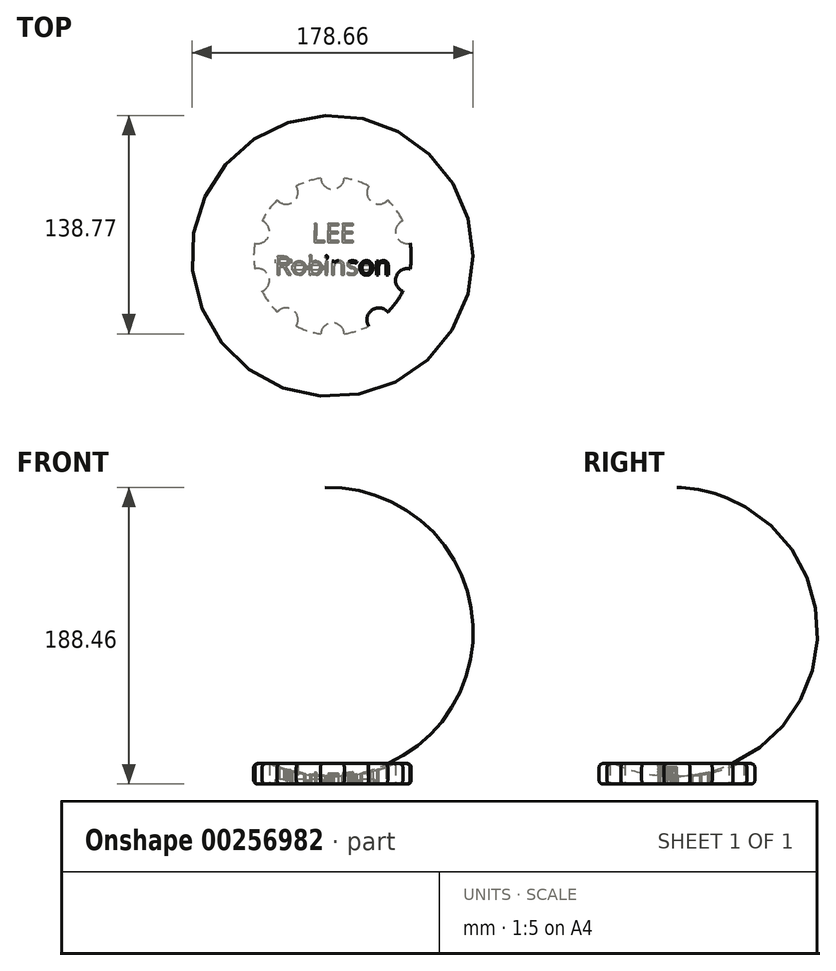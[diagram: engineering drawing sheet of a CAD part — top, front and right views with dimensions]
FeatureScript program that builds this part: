
annotation { "Feature Type Name" : "Feature", "Feature Type Description" : "" }
export const myFeature = defineFeature(function(context is Context, id is Id, definition is map)
    precondition{}
    {
        {
            var Q0;
            Q0=qCreatedBy(makeId("Front.planeOp"),FACE);
            var sketch = newSketch(context, id + "F0", { "sketchPlane" : qUnion([Q0])});
            skLineSegment(sketch, "E0", {"start": v(0, 0) * mm, "end": v(0, 5) * mm});
            skLineSegment(sketch, "E1", {"start": v(-40.53, 13.02) * mm, "end": v(-47.5, 13.02) * mm});
            skLineSegment(sketch, "E2", {"start": v(-50, 10.52) * mm, "end": v(-50, 2.5) * mm});
            skLineSegment(sketch, "E3", {"start": v(-47.5, 0) * mm, "end": v(0, 0) * mm});
            skPoint(sketch, "E4.visualSharp", {"position": v(-50, 13.02) * mm});
            skArc(sketch, "E4.filletArc", {"start": v(-47.5, 13.02) * mm, "mid": v(-49.27, 12.29) * mm, "end": v(-50, 10.52) * mm});
            skPoint(sketch, "E5.visualSharp", {"position": v(-50, 0) * mm});
            skArc(sketch, "E5.filletArc", {"start": v(-50, 2.5) * mm, "mid": v(-49.27, 0.73) * mm, "end": v(-47.5, 0) * mm});
            skArc(sketch, "E6", {"start": v(-39.52, 12.8) * mm, "mid": v(-20.2, 6.7) * mm, "end": v(0, 5) * mm});
            skPoint(sketch, "E7.visualSharp", {"position": v(-40, 13.02) * mm});
            skArc(sketch, "E7.filletArc", {"start": v(-39.52, 12.8) * mm, "mid": v(-40.02, 12.96) * mm, "end": v(-40.53, 13.02) * mm});
            skSolve(sketch);
        }
        {
            var Q0;
            Q0=makeQuery(id+"F0.imprint","IMPRINT",FACE,{"disambiguationData":[TD([[makeQuery(id+"F0.imprint","IMPRINT",EDGE,{"derivedFrom":sQuery(id+"F0.wireOp",EDGE,"E0")}),1.0]])]});
            var Q1;
            Q1=sQuery(id+"F0.wireOp",EDGE,"E0");
            revolve(context, id + "F1", {"entities" : qUnion([Q0]), "axis" : qUnion([Q1]), "revolveType" : RevolveType.FULL});
        }
        {
            var Q0;
            Q0=qCreatedBy(makeId("Top.planeOp"),FACE);
            var sketch = newSketch(context, id + "F2", { "sketchPlane" : qUnion([Q0])});
            skCircle(sketch, "E8", {"center": v(0, -49.99) * mm, "radius": 7.5 * mm});
            skSolve(sketch);
        }
        {
            var Q0;
            Q0=makeQuery(id+"F2.imprint","IMPRINT",FACE,{"disambiguationData":[TD([[makeQuery(id+"F2.imprint","IMPRINT",EDGE,{"derivedFrom":sQuery(id+"F2.wireOp",EDGE,"E8")}),1.0]])]});
            extrude(context, id + "F3", {"entities" : qUnion([Q0]), "operationType" : NewBodyOperationType.REMOVE, "endBound" : BoundingType.THROUGH_ALL, "depth" : 25 * mm});
        }
        {
            var Q0;
            Q0=qCreatedBy(makeId("Front.planeOp"),FACE);
            var sketch = newSketch(context, id + "F4", { "sketchPlane" : qUnion([Q0])});
            skLineSegment(sketch, "E9", {"start": v(0, 0) * mm, "end": v(0, 40.22) * mm});
            skSolve(sketch);
        }
        {
            var Q0;
            Q0=makeQuery(id+"F3.boolean.opBoolean","COPY",FACE,{"derivedFrom":makeQuery(id+"F3.opExtrude","SWEPT_FACE",FACE,{"disambiguationData":[OSD([sQuery(id+"F2.wireOp",EDGE,"E8")])]})});
            var Q1;
            Q1=sQuery(id+"F4.wireOp",EDGE,"E9");
            circularPattern(context, id + "F5", {"patternType" : PatternType.FACE, "faces" : qUnion([Q0]), "axis" : qUnion([Q1]), "angle" : 360 * degree, "instanceCount" : 10, "oppositeDirection" : true, "equalSpace" : true});
        }
        {
            var Q0;
            Q0=qCreatedBy(makeId("Top.planeOp"),FACE);
            var sketch = newSketch(context, id + "F6", { "sketchPlane" : qUnion([Q0])});
            skText(sketch, "E10", { "text": "LEE", "fontName": "OpenSans-Regular.ttf"});
            const initialGuessF6  = {"E10": [-0.01318, 0.0087, 1, 0, 0.012]};
            skSetInitialGuess(sketch, initialGuessF6);
            skSolve(sketch);
        }
        {
            var Q0;
            Q0=qCreatedBy(makeId("Top.planeOp"),FACE);
            var sketch = newSketch(context, id + "F7", { "sketchPlane" : qUnion([Q0])});
            skText(sketch, "E11", { "text": "Robinson\n", "fontName": "OpenSans-Regular.ttf"});
            const initialGuessF7  = {"E11": [-0.0365, -0.012, 1, 0, 0.012]};
            skSetInitialGuess(sketch, initialGuessF7);
            skSolve(sketch);
        }
        {
            var Q0;
            Q0 = qSketchRegion(id + "F6", true);
            extrude(context, id + "F8", {"entities" : qUnion([Q0]), "operationType" : NewBodyOperationType.REMOVE, "depth" : 25 * mm});
        }
        {
            var Q0;
            Q0 = qSketchRegion(id + "F7", true);
            extrude(context, id + "F9", {"entities" : qUnion([Q0]), "operationType" : NewBodyOperationType.REMOVE, "depth" : 25 * mm});
        }
        {
            var Q0;
            Q0=qCreatedBy(makeId("Top.planeOp"),FACE);
            var sketch = newSketch(context, id + "F10", { "sketchPlane" : qUnion([Q0])});
            skLineSegment(sketch, "E12.bottom", {"start": v(26.57, -6.13) * mm, "end": v(16.68, -6.13) * mm});
            skLineSegment(sketch, "E12.top", {"start": v(26.57, -8.94) * mm, "end": v(16.68, -8.94) * mm});
            skLineSegment(sketch, "E12.left", {"start": v(26.57, -6.13) * mm, "end": v(26.57, -8.94) * mm});
            skLineSegment(sketch, "E12.right", {"start": v(16.68, -6.13) * mm, "end": v(16.68, -8.94) * mm});
            skLineSegment(sketch, "E13.bottom", {"start": v(-6.14, -6.02) * mm, "end": v(-15.47, -6.02) * mm});
            skLineSegment(sketch, "E13.top", {"start": v(-6.14, -8.94) * mm, "end": v(-15.47, -8.94) * mm});
            skLineSegment(sketch, "E13.left", {"start": v(-6.14, -6.02) * mm, "end": v(-6.14, -8.94) * mm});
            skLineSegment(sketch, "E13.right", {"start": v(-15.47, -6.02) * mm, "end": v(-15.47, -8.94) * mm});
            skLineSegment(sketch, "E14.bottom", {"start": v(-16.6, -6.02) * mm, "end": v(-26.15, -6.02) * mm});
            skLineSegment(sketch, "E14.top", {"start": v(-16.6, -8.94) * mm, "end": v(-26.15, -8.94) * mm});
            skLineSegment(sketch, "E14.left", {"start": v(-16.6, -6.02) * mm, "end": v(-16.6, -8.94) * mm});
            skLineSegment(sketch, "E14.right", {"start": v(-26.15, -6.02) * mm, "end": v(-26.15, -8.94) * mm});
            skPoint(sketch, "E15.firstSnap0", {"position": v(-26.15, -7.48) * mm});
            skLineSegment(sketch, "E15.bottom", {"start": v(-26.15, -2.31) * mm, "end": v(-36.5, -2.31) * mm});
            skLineSegment(sketch, "E15.top", {"start": v(-26.15, -4.33) * mm, "end": v(-36.5, -4.33) * mm});
            skLineSegment(sketch, "E15.left", {"start": v(-26.15, -2.31) * mm, "end": v(-26.15, -4.33) * mm});
            skLineSegment(sketch, "E15.right", {"start": v(-36.5, -2.31) * mm, "end": v(-36.5, -4.33) * mm});
            skSolve(sketch);
        }
        {
            var Q0;
            Q0=makeQuery(id+"F10.imprint","IMPRINT",FACE,{"disambiguationData":[TD([[makeQuery(id+"F10.imprint","IMPRINT",EDGE,{"derivedFrom":sQuery(id+"F10.wireOp",EDGE,"E12.bottom")}),1.0]])]});
            var Q1;
            Q1=makeQuery(id+"F10.imprint","IMPRINT",FACE,{"disambiguationData":[TD([[makeQuery(id+"F10.imprint","IMPRINT",EDGE,{"derivedFrom":sQuery(id+"F10.wireOp",EDGE,"E13.bottom")}),1.0]])]});
            var Q2;
            Q2=makeQuery(id+"F10.imprint","IMPRINT",FACE,{"disambiguationData":[TD([[makeQuery(id+"F10.imprint","IMPRINT",EDGE,{"derivedFrom":sQuery(id+"F10.wireOp",EDGE,"E14.bottom")}),1.0]])]});
            var Q3;
            Q3=makeQuery(id+"F10.imprint","IMPRINT",FACE,{"disambiguationData":[TD([[makeQuery(id+"F10.imprint","IMPRINT",EDGE,{"derivedFrom":sQuery(id+"F10.wireOp",EDGE,"E15.bottom")}),1.0]])]});
            extrude(context, id + "F11", {"entities" : qUnion([Q0, Q1, Q2, Q3]), "depth" : 3 * mm});
        }
    });
